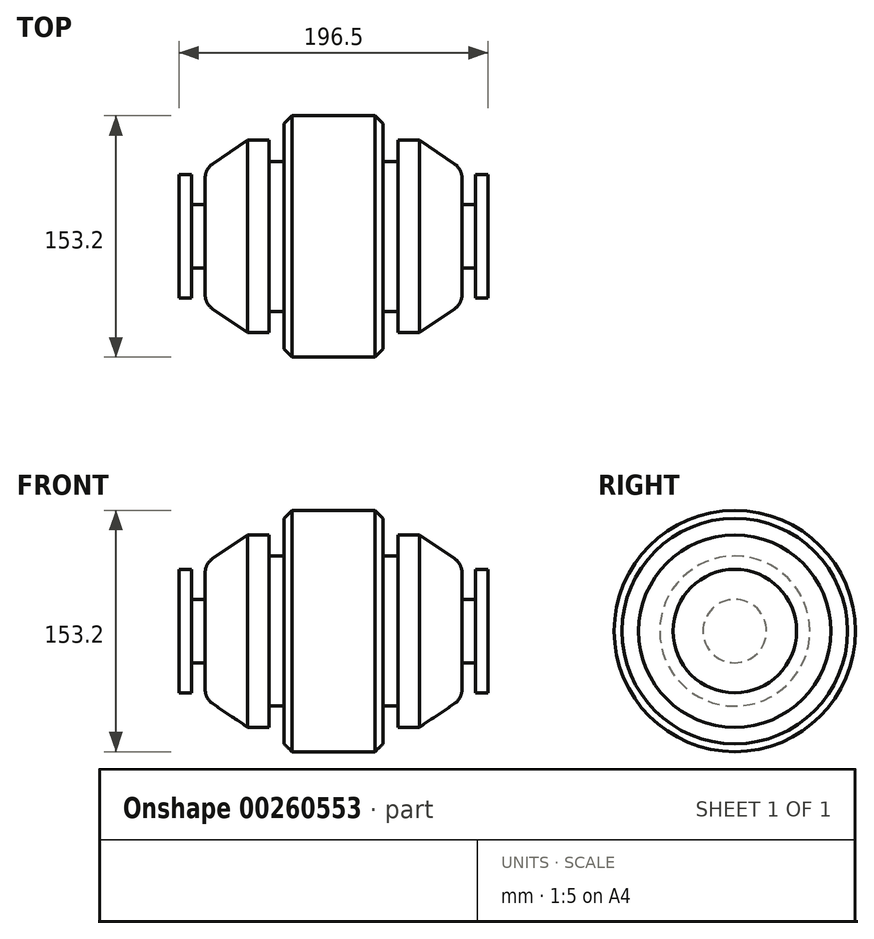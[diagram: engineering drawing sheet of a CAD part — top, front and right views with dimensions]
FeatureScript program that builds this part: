
annotation { "Feature Type Name" : "Feature", "Feature Type Description" : "" }
export const myFeature = defineFeature(function(context is Context, id is Id, definition is map)
    precondition{}
    {
        {
            var Q0;
            Q0=qCreatedBy(makeId("Front.planeOp"),FACE);
            var sketch = newSketch(context, id + "F0", { "sketchPlane" : qUnion([Q0])});
            skLineSegment(sketch, "E0", {"start": v(0, 0) * mm, "end": v(-98.25, 0) * mm});
            skLineSegment(sketch, "E1", {"start": v(-98.25, 0) * mm, "end": v(-98.25, 39.27) * mm});
            skLineSegment(sketch, "E2", {"start": v(-98.25, 39.27) * mm, "end": v(-90.18, 39.27) * mm});
            skLineSegment(sketch, "E3", {"start": v(-90.18, 39.27) * mm, "end": v(-90.18, 20.16) * mm});
            skLineSegment(sketch, "E4", {"start": v(-90.18, 20.16) * mm, "end": v(-81.52, 20.16) * mm});
            skLineSegment(sketch, "E5", {"start": v(-81.52, 20.16) * mm, "end": v(-81.52, 42.85) * mm});
            skLineSegment(sketch, "E6", {"start": v(-81.52, 42.85) * mm, "end": v(-54.65, 61.07) * mm});
            skLineSegment(sketch, "E7", {"start": v(-54.65, 61.07) * mm, "end": v(-40.91, 61.07) * mm});
            skLineSegment(sketch, "E8", {"start": v(-40.91, 61.07) * mm, "end": v(-40.91, 47.63) * mm});
            skLineSegment(sketch, "E9", {"start": v(-40.91, 47.63) * mm, "end": v(-31.36, 47.63) * mm});
            skLineSegment(sketch, "E10", {"start": v(-31.36, 47.63) * mm, "end": v(-31.36, 76.6) * mm});
            skLineSegment(sketch, "E11", {"start": v(-31.36, 76.6) * mm, "end": v(0, 76.6) * mm});
            skLineSegment(sketch, "E12", {"start": v(0, 76.6) * mm, "end": v(0, 0) * mm});
            skSolve(sketch);
        }
        {
            var Q0;
            Q0=makeQuery(id+"F0.imprint","IMPRINT",FACE,{"disambiguationData":[TD([[makeQuery(id+"F0.imprint","IMPRINT",EDGE,{"derivedFrom":sQuery(id+"F0.wireOp",EDGE,"E0")}),-1.0]])]});
            var Q1;
            Q1=sQuery(id+"F0.wireOp",EDGE,"E0");
            revolve(context, id + "F1", {"entities" : qUnion([Q0]), "axis" : qUnion([Q1]), "revolveType" : RevolveType.FULL});
        }
        {
            var Q0;
            Q0=makeQuery(id+"F1.opRevolve","SWEPT_EDGE",EDGE,{"disambiguationData":[OSD([sQuery(id+"F0.wireOp",EDGE,"E5"),sQuery(id+"F0.wireOp",EDGE,"E6")])]});
            fillet(context, id + "F2", {"entities" : qUnion([Q0]), "radius" : 10.6 * mm, "tangentPropagation" : true, "allowEdgeOverflow" : false});
        }
        {
            var Q0;
            Q0=makeQuery(id+"F1.opRevolve","SWEPT_EDGE",EDGE,{"disambiguationData":[OSD([sQuery(id+"F0.wireOp",EDGE,"E10"),sQuery(id+"F0.wireOp",EDGE,"E11")])]});
            chamfer(context, id + "F3", {"entities" : qUnion([Q0]), "width" : 5 * mm, "tangentPropagation" : true});
        }
        {
            var Q0;
            Q0=makeQuery(id+"F1.opRevolve","SWEPT_BODY",BODY,{"disambiguationData":[OSD([sQuery(id+"F0.wireOp",EDGE,"E0"),sQuery(id+"F0.wireOp",EDGE,"E1"),sQuery(id+"F0.wireOp",EDGE,"E2"),sQuery(id+"F0.wireOp",EDGE,"E3"),sQuery(id+"F0.wireOp",EDGE,"E4"),sQuery(id+"F0.wireOp",EDGE,"E5"),sQuery(id+"F0.wireOp",EDGE,"E6"),sQuery(id+"F0.wireOp",EDGE,"E7"),sQuery(id+"F0.wireOp",EDGE,"E8"),sQuery(id+"F0.wireOp",EDGE,"E9"),sQuery(id+"F0.wireOp",EDGE,"E10"),sQuery(id+"F0.wireOp",EDGE,"E11"),sQuery(id+"F0.wireOp",EDGE,"E12")])]});
            var Q1;
            Q1=qCreatedBy(makeId("Right.planeOp"),FACE);
            mirror(context, id + "F4", {"operationType" : NewBodyOperationType.ADD, "entities" : qUnion([Q0]), "mirrorPlane" : qUnion([Q1])});
        }
    });
